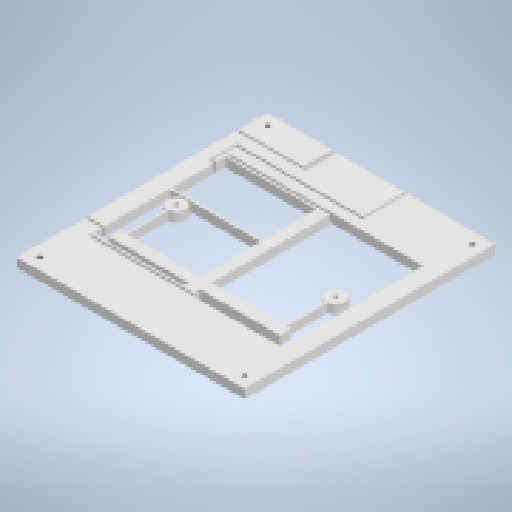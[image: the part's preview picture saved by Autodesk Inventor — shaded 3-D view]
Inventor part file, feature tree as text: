
AUTODESK INVENTOR PART (.ipt)
format: ipt  version: 2023 (Build 270158000, 158)  size: 290,816 bytes
history: native  units: mm
features: extrude x4, thread x4, sketch x4
ambient origin geometry x8: Origin, YZ Plane, XZ Plane, XY Plane, X Axis, Y Axis, Z Axis, Center Point
bodies: Solid1 (feature_tree)
feature tree (12):
  extrude  "Extrusion1"  Depth=100.0mm
  extrude  "Extrusion4"  Depth=5.0mm
  thread  "Thread7"  [1 undecoded]
  thread  "Thread8"  [1 undecoded]
  thread  "Thread9"  [1 undecoded]
  thread  "Thread10"  [1 undecoded]
  extrude  "Extrusion5"  Depth=10.0mm TaperAngle=0.0deg
  extrude  "Extrusion6"  Depth=10.0mm
  sketch  "Sketch1"  dims[d0=110.0mm d1=100.0mm]
  sketch  "Sketch5"  dims[d2=4.0mm d3=0.0mm d41=5.0mm d42=5.0mm d43=2.2mm d44=10.0mm d45=0.0mm d46=10.0mm d47=0.0mm]
  sketch  "Sketch6"  dims[d48=10.0mm d49=0.0mm d50=10.0mm d51=0.0mm]
  sketch  "Sketch8"  dims[d52=10.0mm d53=0.0mm d66=10.0mm d91=12.0mm d92=4.0mm d93=0.0mm d103=1.0mm d113=50.0mm d115=5.0mm d117=1.0mm d119=40.0mm d121=40.0mm d122=1.0mm d140=2.2mm d141=40.0mm d142=1.0mm d143=1.0mm d151=1.0mm d153=5.0mm d154=5.0mm d155=5.0mm d156=5.0mm d157=30.0mm d158=1.0mm d159=1.0mm d160=1.0mm d161=1.0mm d162=1.0mm d163=4.0mm d164=0.0mm d166=35.0mm d167=55.0mm d168=35.0mm d169=5.0mm d170=2.0mm d171=8.0mm d172=1.0mm d173=0.0mm]
note: 4 required parameter values undecoded (feature->parameter linkage not recoverable at this tier; creation-order binding heuristic only, values carry confidence <= 0.55)
